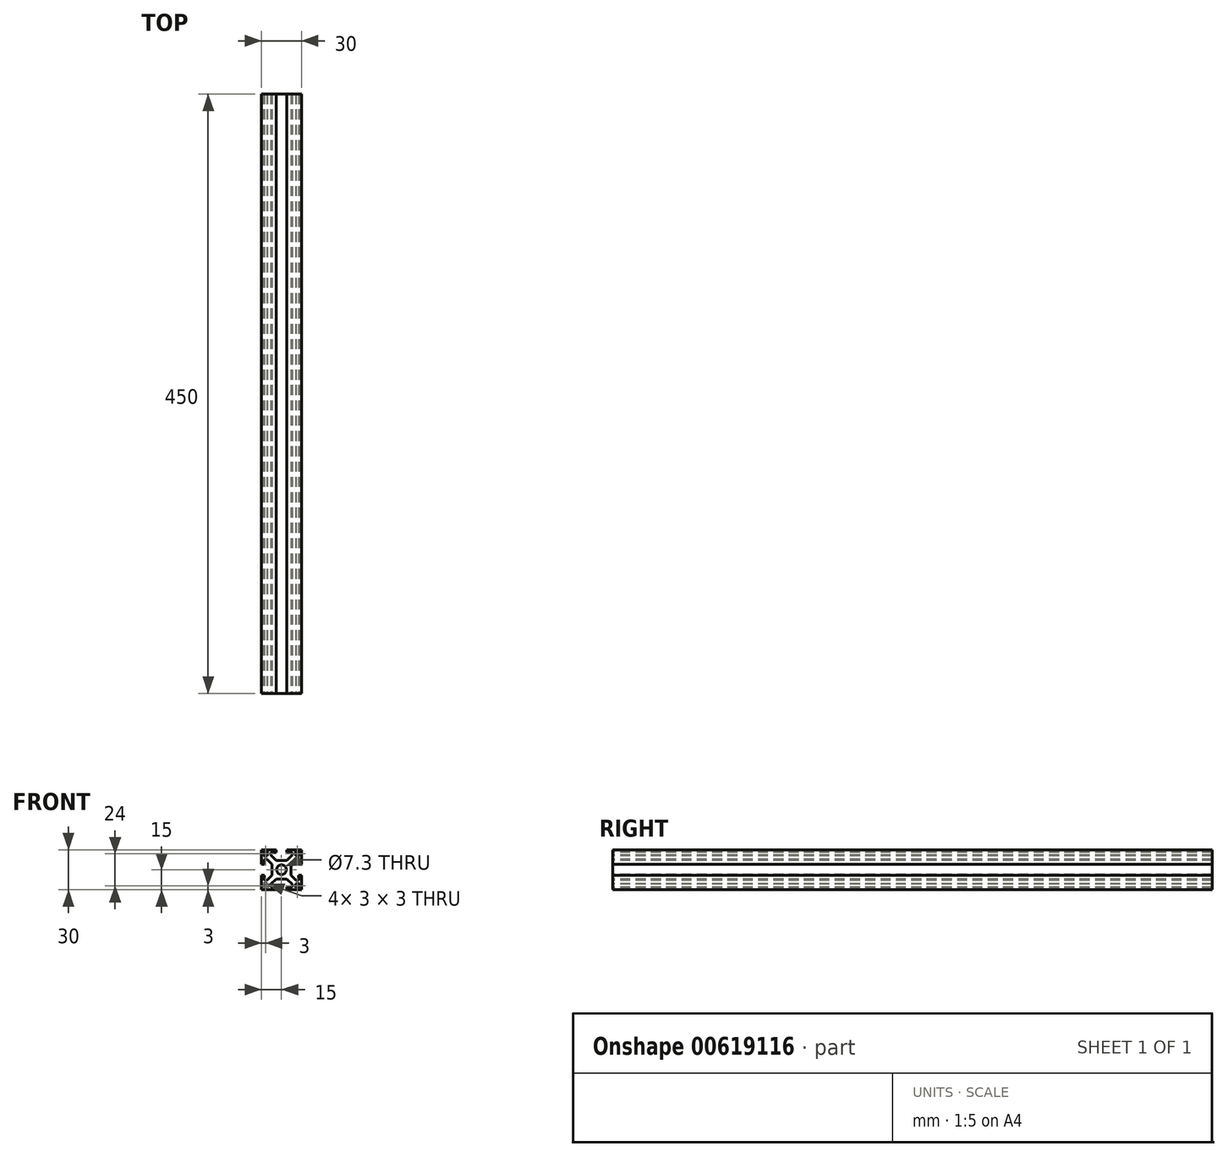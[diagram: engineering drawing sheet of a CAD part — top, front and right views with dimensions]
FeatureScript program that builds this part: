
annotation { "Feature Type Name" : "Feature", "Feature Type Description" : "" }
export const myFeature = defineFeature(function(context is Context, id is Id, definition is map)
    precondition{}
    {
        {
            var Q0;
            Q0=qCreatedBy(makeId("Front.planeOp"),FACE);
            var sketch = newSketch(context, id + "F0", { "sketchPlane" : qUnion([Q0])});
            skLineSegment(sketch, "E0.bottom", {"start": v(-15, 15) * mm, "end": v(15, 15) * mm});
            skLineSegment(sketch, "E0.top", {"start": v(-15, -15) * mm, "end": v(15, -15) * mm});
            skLineSegment(sketch, "E0.left", {"start": v(-15, 15) * mm, "end": v(-15, -15) * mm});
            skLineSegment(sketch, "E0.right", {"start": v(15, 15) * mm, "end": v(15, -15) * mm});
            skPoint(sketch, "E0.middle", {"position": v(0, 0) * mm});
            skSolve(sketch);
        }
        {
            var Q0;
            Q0=qSketchRegion(id+"F0",true);
            extrude(context, id + "F1", {"entities" : qUnion([Q0]), "depth" : 450 * mm, "offsetDistance" : 25 * mm});
        }
        {
            var Q0;
            Q0=makeQuery(id+"F1.opExtrude","CAP_FACE",FACE,{"disambiguationData":[OSD([sQuery(id+"F0.wireOp",EDGE,"E0.bottom"),sQuery(id+"F0.wireOp",EDGE,"E0.top"),sQuery(id+"F0.wireOp",EDGE,"E0.left"),sQuery(id+"F0.wireOp",EDGE,"E0.right")])],"isStart":false});
            var sketch = newSketch(context, id + "F2", { "sketchPlane" : qUnion([Q0])});
            skLineSegment(sketch, "E1", {"start": v(-15, 4) * mm, "end": v(-13, 4) * mm});
            skLineSegment(sketch, "E2", {"start": v(-13, 4) * mm, "end": v(-13, 8) * mm});
            skLineSegment(sketch, "E3", {"start": v(-13, 8) * mm, "end": v(-11, 8) * mm});
            skLineSegment(sketch, "E4", {"start": v(-11, 8) * mm, "end": v(-7, 4) * mm});
            skLineSegment(sketch, "E5", {"start": v(-7, 4) * mm, "end": v(-7, -4) * mm});
            skLineSegment(sketch, "E6", {"start": v(-7, -4) * mm, "end": v(-11, -8) * mm});
            skLineSegment(sketch, "E7", {"start": v(-11, -8) * mm, "end": v(-13, -8) * mm});
            skLineSegment(sketch, "E8", {"start": v(-13, -8) * mm, "end": v(-13, -4) * mm});
            skLineSegment(sketch, "E9", {"start": v(-13, -4) * mm, "end": v(-15, -4) * mm});
            skLineSegment(sketch, "E10", {"start": v(-15, -4) * mm, "end": v(-15, 4) * mm});
            skLineSegment(sketch, "E11", {"start": v(-4, 15) * mm, "end": v(4, 15) * mm});
            skLineSegment(sketch, "E12", {"start": v(4, 15) * mm, "end": v(4, 13) * mm});
            skLineSegment(sketch, "E13", {"start": v(4, 13) * mm, "end": v(8, 13) * mm});
            skLineSegment(sketch, "E14", {"start": v(8, 13) * mm, "end": v(8, 11) * mm});
            skLineSegment(sketch, "E15", {"start": v(8, 11) * mm, "end": v(4, 7) * mm});
            skLineSegment(sketch, "E16", {"start": v(4, 7) * mm, "end": v(-4, 7) * mm});
            skLineSegment(sketch, "E17", {"start": v(-4, 7) * mm, "end": v(-8, 11) * mm});
            skLineSegment(sketch, "E18", {"start": v(-8, 11) * mm, "end": v(-8, 13) * mm});
            skLineSegment(sketch, "E19", {"start": v(-8, 13) * mm, "end": v(-4, 13) * mm});
            skLineSegment(sketch, "E20", {"start": v(-4, 13) * mm, "end": v(-4, 15) * mm});
            skLineSegment(sketch, "E21", {"start": v(15, -4) * mm, "end": v(15, 4) * mm});
            skLineSegment(sketch, "E22", {"start": v(15, 4) * mm, "end": v(13, 4) * mm});
            skLineSegment(sketch, "E23", {"start": v(13, 4) * mm, "end": v(13, 8) * mm});
            skLineSegment(sketch, "E24", {"start": v(13, 8) * mm, "end": v(11, 8) * mm});
            skLineSegment(sketch, "E25", {"start": v(11, 8) * mm, "end": v(7, 4) * mm});
            skLineSegment(sketch, "E26", {"start": v(7, 4) * mm, "end": v(7, -4) * mm});
            skLineSegment(sketch, "E27", {"start": v(7, -4) * mm, "end": v(11, -8) * mm});
            skLineSegment(sketch, "E28", {"start": v(11, -8) * mm, "end": v(13, -8) * mm});
            skLineSegment(sketch, "E29", {"start": v(13, -8) * mm, "end": v(13, -4) * mm});
            skLineSegment(sketch, "E30", {"start": v(13, -4) * mm, "end": v(15, -4) * mm});
            skCircle(sketch, "E31", {"center": v(0, 0) * mm, "radius": 3.65 * mm});
            skLineSegment(sketch, "E32", {"start": v(-4, -15) * mm, "end": v(4, -15) * mm});
            skPoint(sketch, "E32.endSnap0", {"position": v(4, 14) * mm});
            skLineSegment(sketch, "E33", {"start": v(4, -15) * mm, "end": v(3.95, -12.94) * mm});
            skLineSegment(sketch, "E34", {"start": v(3.95, -12.94) * mm, "end": v(8, -12.94) * mm});
            skLineSegment(sketch, "E35", {"start": v(8, -12.94) * mm, "end": v(8, -10.94) * mm});
            skLineSegment(sketch, "E36", {"start": v(8, -10.94) * mm, "end": v(4, -6.94) * mm});
            skLineSegment(sketch, "E37", {"start": v(4, -6.94) * mm, "end": v(-4, -6.94) * mm});
            skLineSegment(sketch, "E38", {"start": v(-4, -6.94) * mm, "end": v(-8, -10.94) * mm});
            skLineSegment(sketch, "E39", {"start": v(-8, -10.94) * mm, "end": v(-8, -12.94) * mm});
            skLineSegment(sketch, "E40", {"start": v(-8, -12.94) * mm, "end": v(-4, -12.94) * mm});
            skLineSegment(sketch, "E41", {"start": v(-4, -12.94) * mm, "end": v(-4, -15) * mm});
            skLineSegment(sketch, "E42.bottom", {"start": v(10.5, 13.5) * mm, "end": v(13.5, 13.5) * mm});
            skLineSegment(sketch, "E42.top", {"start": v(10.5, 10.5) * mm, "end": v(13.5, 10.5) * mm});
            skLineSegment(sketch, "E42.left", {"start": v(10.5, 13.5) * mm, "end": v(10.5, 10.5) * mm});
            skLineSegment(sketch, "E42.right", {"start": v(13.5, 13.5) * mm, "end": v(13.5, 10.5) * mm});
            skPoint(sketch, "E42.middle", {"position": v(12, 12) * mm});
            skLineSegment(sketch, "E43.bottom", {"start": v(-13.5, 13.5) * mm, "end": v(-10.5, 13.5) * mm});
            skLineSegment(sketch, "E43.top", {"start": v(-13.5, 10.5) * mm, "end": v(-10.5, 10.5) * mm});
            skLineSegment(sketch, "E43.left", {"start": v(-13.5, 13.5) * mm, "end": v(-13.5, 10.5) * mm});
            skLineSegment(sketch, "E43.right", {"start": v(-10.5, 13.5) * mm, "end": v(-10.5, 10.5) * mm});
            skPoint(sketch, "E43.middle", {"position": v(-12, 12) * mm});
            skLineSegment(sketch, "E44.bottom", {"start": v(13.5, -13.5) * mm, "end": v(10.5, -13.5) * mm});
            skLineSegment(sketch, "E44.top", {"start": v(13.5, -10.5) * mm, "end": v(10.5, -10.5) * mm});
            skLineSegment(sketch, "E44.left", {"start": v(13.5, -13.5) * mm, "end": v(13.5, -10.5) * mm});
            skLineSegment(sketch, "E44.right", {"start": v(10.5, -13.5) * mm, "end": v(10.5, -10.5) * mm});
            skPoint(sketch, "E44.middle", {"position": v(12, -12) * mm});
            skLineSegment(sketch, "E45.bottom", {"start": v(-13.5, -13.5) * mm, "end": v(-10.5, -13.5) * mm});
            skLineSegment(sketch, "E45.top", {"start": v(-13.5, -10.5) * mm, "end": v(-10.5, -10.5) * mm});
            skLineSegment(sketch, "E45.left", {"start": v(-13.5, -13.5) * mm, "end": v(-13.5, -10.5) * mm});
            skLineSegment(sketch, "E45.right", {"start": v(-10.5, -13.5) * mm, "end": v(-10.5, -10.5) * mm});
            skPoint(sketch, "E45.middle", {"position": v(-12, -12) * mm});
            skSolve(sketch);
        }
        {
            var Q0;
            Q0=qSketchRegion(id+"F2",true);
            extrude(context, id + "F3", {"entities" : qUnion([Q0]), "operationType" : NewBodyOperationType.REMOVE, "endBound" : BoundingType.THROUGH_ALL, "oppositeDirection" : true, "depth" : 25 * mm, "offsetDistance" : 25 * mm});
        }
    });
